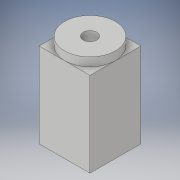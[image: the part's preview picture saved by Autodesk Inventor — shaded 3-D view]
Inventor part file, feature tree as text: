
AUTODESK INVENTOR PART (.ipt)
format: ipt  version: 2019 (Build 230136000, 136)  size: 123,392 bytes
history: native  units: mm
features: extrude x3, sketch x3, other x1
ambient origin geometry x8: Origin, YZ Plane, XZ Plane, XY Plane, X Axis, Y Axis, Z Axis, Center Point
bodies: Body1 (feature_tree)
feature tree (7):
  other  "Sólido1"
  extrude  "Extrusión1"  Depth=30.0mm
  extrude  "Extrusión2"  Depth=50.0mm TaperAngle=0.0deg
  extrude  "Extrusión3"  Depth=5.0mm TaperAngle=0.0deg
  sketch  "Boceto1"  dims[d0=30.0mm d1=30.0mm]
  sketch  "Boceto2"  dims[d2=8.0mm d3=50.0mm d4=0.0mm]
  sketch  "Boceto3"  dims[d5=30.0mm d6=5.0mm d7=0.0mm d8=11.0mm d9=26.0mm d10=26.0mm d11=46.0mm d12=0.0mm]
